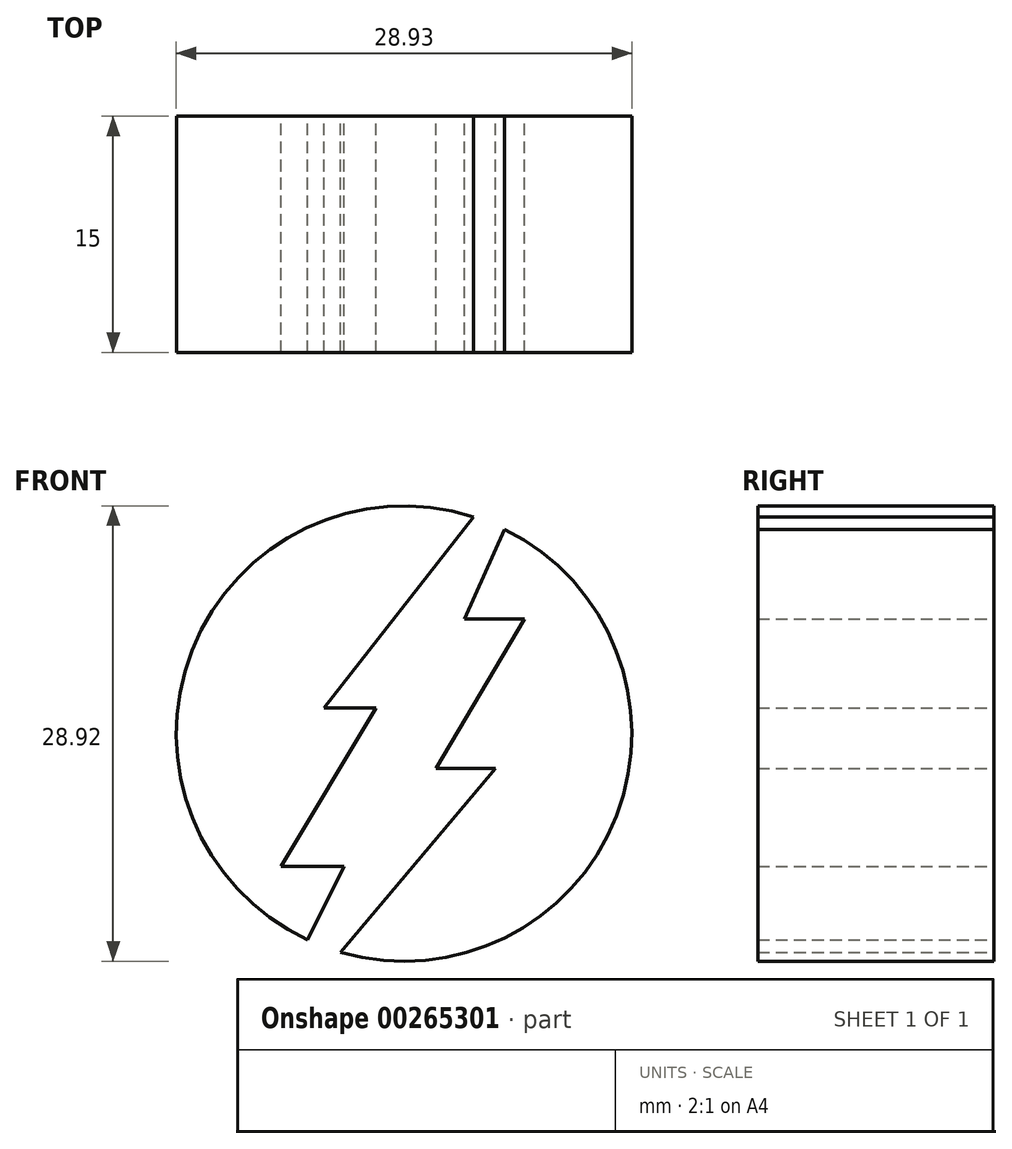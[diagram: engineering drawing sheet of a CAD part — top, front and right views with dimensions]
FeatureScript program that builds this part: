
annotation { "Feature Type Name" : "Feature", "Feature Type Description" : "" }
export const myFeature = defineFeature(function(context is Context, id is Id, definition is map)
    precondition{}
    {
        {
            var Q0;
            Q0=qCreatedBy(makeId("Front.planeOp"),FACE);
            var sketch = newSketch(context, id + "F0", { "sketchPlane" : qUnion([Q0])});
            skArc(sketch, "E0", {"start": v(-137, 9.44) * mm, "mid": v(-154.87, 0.94) * mm, "end": v(-147.52, -17.43) * mm});
            skPoint(sketch, "E0.first.point", {"position": v(-138.47, 9.83) * mm});
            skPoint(sketch, "E0.second.point", {"position": v(-134.4, -16.98) * mm});
            skPoint(sketch, "E0.third.point", {"position": v(-154.07, -11.31) * mm});
            skLineSegment(sketch, "E1", {"start": v(-131.48, 16.5) * mm, "end": v(-146.5, -2.71) * mm});
            skLineSegment(sketch, "E2", {"start": v(-146.5, -2.71) * mm, "end": v(-143.18, -2.71) * mm});
            skLineSegment(sketch, "E3", {"start": v(-143.18, -2.71) * mm, "end": v(-149.22, -12.78) * mm});
            skLineSegment(sketch, "E4", {"start": v(-149.22, -12.78) * mm, "end": v(-145.22, -12.78) * mm});
            skLineSegment(sketch, "E5", {"start": v(-145.22, -12.78) * mm, "end": v(-151.46, -25.38) * mm});
            skLineSegment(sketch, "E6", {"start": v(-151.46, -25.38) * mm, "end": v(-135.6, -6.54) * mm});
            skLineSegment(sketch, "E7", {"start": v(-135.6, -6.54) * mm, "end": v(-139.36, -6.54) * mm});
            skLineSegment(sketch, "E8", {"start": v(-139.36, -6.54) * mm, "end": v(-133.75, 2.95) * mm});
            skLineSegment(sketch, "E9", {"start": v(-133.75, 2.95) * mm, "end": v(-137.58, 2.95) * mm});
            skLineSegment(sketch, "E10", {"start": v(-137.58, 2.95) * mm, "end": v(-131.48, 16.5) * mm});
            skArc(sketch, "E11.trimOffspring", {"start": v(-145.43, -18.22) * mm, "mid": v(-127.92, -9.56) * mm, "end": v(-135.01, 8.64) * mm});
            skSolve(sketch);
        }
        {
            var Q0;
            {var subQ2=sQuery(id+"F0.wireOp",EDGE,"E0");Q0=makeQuery(id+"F0.imprint","IMPRINT",FACE,{"disambiguationData":[TD([[makeQuery(id+"F0.imprint","IMPRINT",EDGE,{"derivedFrom":subQ2}),1.0]])]});}
            var Q1;
            {var subQ1=sQuery(id+"F0.wireOp",EDGE,"E7");Q1=makeQuery(id+"F0.imprint","IMPRINT",FACE,{"disambiguationData":[TD([[makeQuery(id+"F0.imprint","IMPRINT",EDGE,{"derivedFrom":subQ1}),-1.0]])]});}
            extrude(context, id + "F1", {"entities" : qUnion([Q0, Q1]), "offsetDistance" : 25 * mm, "depth" : 15 * mm});
        }
    });
